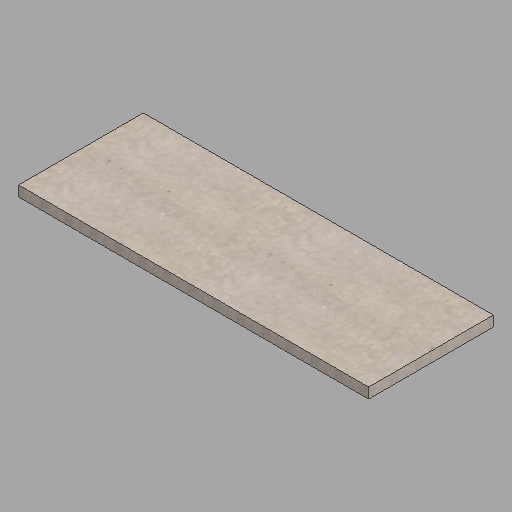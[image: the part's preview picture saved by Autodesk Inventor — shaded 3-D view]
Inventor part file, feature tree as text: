
AUTODESK INVENTOR PART (.ipt)
format: ipt  version: 2022.1 (Build 261234020, 234B)  size: 193,024 bytes
history: native  units: in
note: dims shown in document units (in); Inventor stores cm internally (conversion verified against a paired STEP export)
features: other x1, extrude x1, sketch x1
ambient origin geometry x8: Origin, YZ Plane, XZ Plane, XY Plane, X Axis, Y Axis, Z Axis, Center Point
bodies: Body1 (feature_tree)
feature tree (3):
  other  "Lid Stone"
  extrude  "Extrusion1"  Depth=36.0in
  sketch  "Sketch1"  dims[d0=101.0in d1=36.0in d2=3.0in d3=0.0in]
